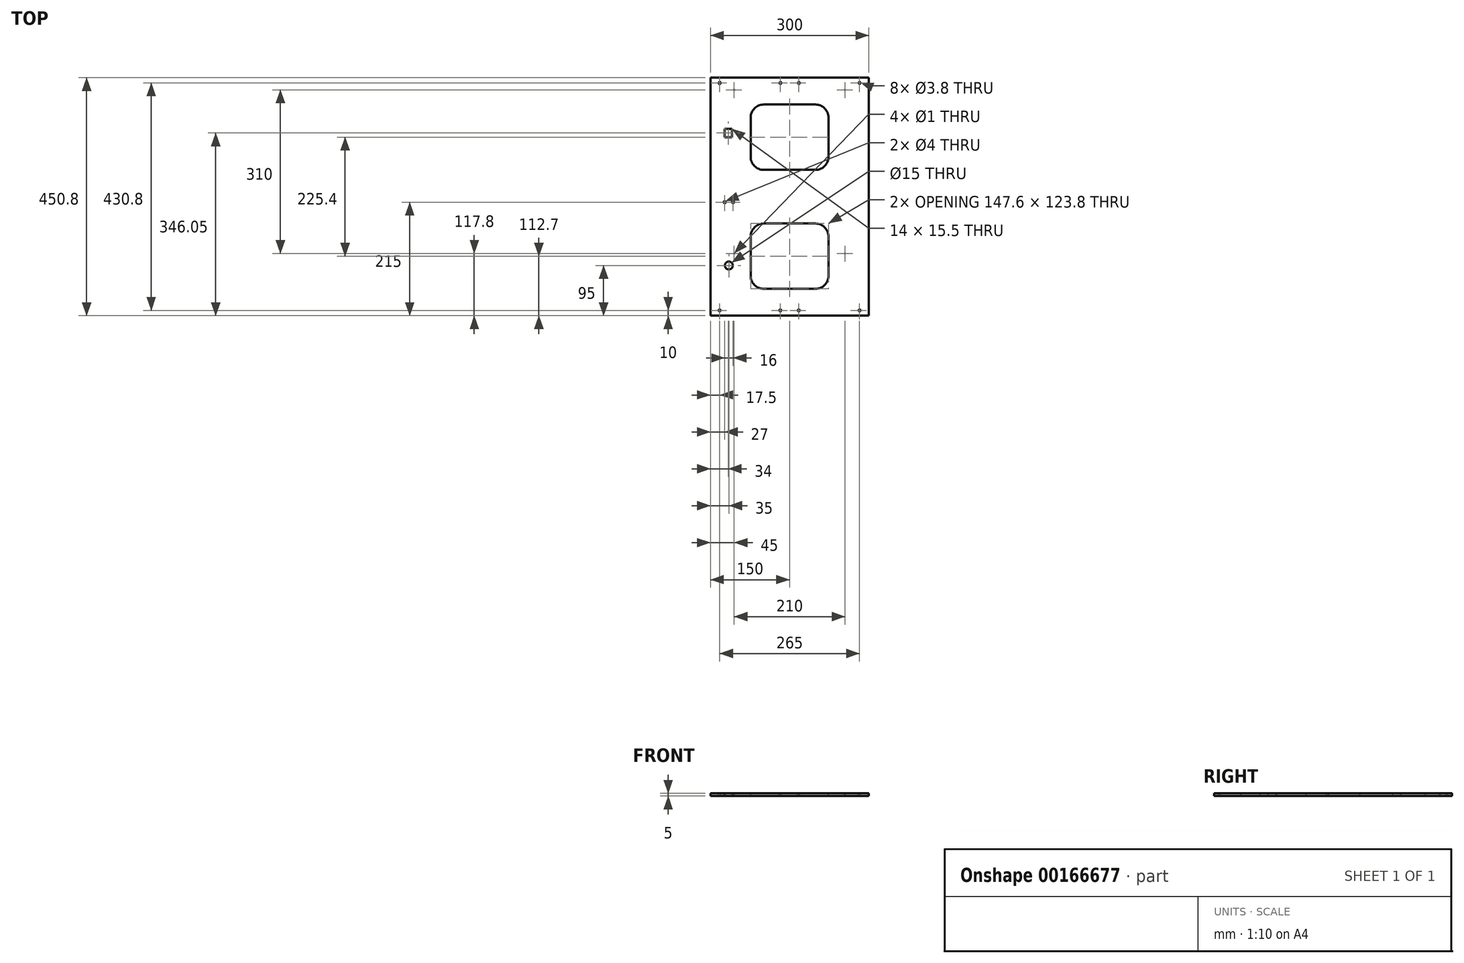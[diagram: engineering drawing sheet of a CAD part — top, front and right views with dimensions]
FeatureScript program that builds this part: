
annotation { "Feature Type Name" : "Feature", "Feature Type Description" : "" }
export const myFeature = defineFeature(function(context is Context, id is Id, definition is map)
    precondition{}
    {
        {
            var Q0;
            Q0=qCreatedBy(makeId("Top.planeOp"),FACE);
            var sketch = newSketch(context, id + "F0", { "sketchPlane" : qUnion([Q0])});
            skLineSegment(sketch, "E0.bottom", {"start": v(-150, 225.4) * mm, "end": v(150, 225.4) * mm});
            skLineSegment(sketch, "E0.top", {"start": v(-150, -225.4) * mm, "end": v(150, -225.4) * mm});
            skLineSegment(sketch, "E0.left", {"start": v(-150, 225.4) * mm, "end": v(-150, -225.4) * mm});
            skLineSegment(sketch, "E0.right", {"start": v(150, 225.4) * mm, "end": v(150, -225.4) * mm});
            skLineSegment(sketch, "E1.bottom", {"start": v(-132.5, 215.4) * mm, "end": v(132.5, 215.4) * mm, "construction": true});
            skLineSegment(sketch, "E1.top", {"start": v(-132.5, -215.4) * mm, "end": v(132.5, -215.4) * mm, "construction": true});
            skLineSegment(sketch, "E1.left", {"start": v(-132.5, 215.4) * mm, "end": v(-132.5, -215.4) * mm, "construction": true});
            skLineSegment(sketch, "E1.right", {"start": v(132.5, 215.4) * mm, "end": v(132.5, -215.4) * mm, "construction": true});
            skCircle(sketch, "E2", {"center": v(132.5, 215.4) * mm, "radius": 1.9 * mm});
            skCircle(sketch, "E3", {"center": v(132.5, -215.4) * mm, "radius": 1.9 * mm});
            skCircle(sketch, "E4", {"center": v(-132.5, -215.4) * mm, "radius": 1.9 * mm});
            skCircle(sketch, "E5", {"center": v(-132.5, 215.4) * mm, "radius": 1.9 * mm});
            skLineSegment(sketch, "E6.bottom", {"start": v(-17.5, 215.4) * mm, "end": v(17.5, 215.4) * mm, "construction": true});
            skLineSegment(sketch, "E6.top", {"start": v(-17.5, -215.4) * mm, "end": v(17.5, -215.4) * mm});
            skLineSegment(sketch, "E6.left", {"start": v(-17.5, 215.4) * mm, "end": v(-17.5, -215.4) * mm, "construction": true});
            skLineSegment(sketch, "E6.right", {"start": v(17.5, 215.4) * mm, "end": v(17.5, -215.4) * mm, "construction": true});
            skLineSegment(sketch, "E7", {"start": v(-150, 0) * mm, "end": v(150, 0) * mm, "construction": true});
            skCircle(sketch, "E8", {"center": v(-17.5, 215.4) * mm, "radius": 1.9 * mm});
            skCircle(sketch, "E9", {"center": v(17.5, 215.4) * mm, "radius": 1.9 * mm});
            skCircle(sketch, "E10", {"center": v(-17.5, -215.4) * mm, "radius": 1.9 * mm});
            skCircle(sketch, "E11", {"center": v(17.5, -215.4) * mm, "radius": 1.9 * mm});
            skSolve(sketch);
        }
        {
            var Q0;
            Q0=qCreatedBy(makeId("Top.planeOp"),FACE);
            var sketch = newSketch(context, id + "F1", { "sketchPlane" : qUnion([Q0])});
            skLineSegment(sketch, "E12.bottom", {"start": v(-110, 207.4) * mm, "end": v(110, 207.4) * mm, "construction": true});
            skLineSegment(sketch, "E12.top", {"start": v(-110, -112.6) * mm, "end": v(110, -112.6) * mm, "construction": true});
            skLineSegment(sketch, "E12.left", {"start": v(-110, 207.4) * mm, "end": v(-110, -112.6) * mm, "construction": true});
            skLineSegment(sketch, "E12.right", {"start": v(110, 207.4) * mm, "end": v(110, -112.6) * mm, "construction": true});
            skLineSegment(sketch, "E13.bottom", {"start": v(-105, 202.4) * mm, "end": v(105, 202.4) * mm, "construction": true});
            skLineSegment(sketch, "E13.top", {"start": v(-105, -107.6) * mm, "end": v(105, -107.6) * mm, "construction": true});
            skLineSegment(sketch, "E13.left", {"start": v(-105, 202.4) * mm, "end": v(-105, -107.6) * mm, "construction": true});
            skLineSegment(sketch, "E13.right", {"start": v(105, 202.4) * mm, "end": v(105, -107.6) * mm, "construction": true});
            skCircle(sketch, "E14", {"center": v(105, 202.4) * mm, "radius": 0.5 * mm});
            skCircle(sketch, "E15", {"center": v(105, -107.6) * mm, "radius": 0.5 * mm});
            skCircle(sketch, "E16", {"center": v(-105, -107.6) * mm, "radius": 0.5 * mm});
            skCircle(sketch, "E17", {"center": v(-105, 202.4) * mm, "radius": 0.5 * mm});
            skLineSegment(sketch, "E18", {"start": v(-110, 47.4) * mm, "end": v(110, 47.4) * mm, "construction": true});
            skPoint(sketch, "E18.startSnap0", {"position": v(-105, 47.4) * mm});
            skSolve(sketch);
        }
        {
            var Q0;
            Q0=makeQuery(id+"F0.imprint","IMPRINT",FACE,{"disambiguationData":[TD([[makeQuery(id+"F0.imprint","IMPRINT",EDGE,{"derivedFrom":sQuery(id+"F0.wireOp",EDGE,"E0.bottom")}),-1.0]])]});
            extrude(context, id + "F2", {"entities" : qUnion([Q0]), "oppositeDirection" : true, "depth" : 5 * mm});
        }
        {
            var Q0;
            Q0=makeQuery(id+"F1.imprint","IMPRINT",FACE,{"disambiguationData":[TD([[makeQuery(id+"F1.imprint","IMPRINT",EDGE,{"derivedFrom":sQuery(id+"F1.wireOp",EDGE,"E17")}),1.0]])]});
            var Q1;
            Q1=makeQuery(id+"F1.imprint","IMPRINT",FACE,{"disambiguationData":[TD([[makeQuery(id+"F1.imprint","IMPRINT",EDGE,{"derivedFrom":sQuery(id+"F1.wireOp",EDGE,"E14")}),1.0]])]});
            var Q2;
            Q2=makeQuery(id+"F1.imprint","IMPRINT",FACE,{"disambiguationData":[TD([[makeQuery(id+"F1.imprint","IMPRINT",EDGE,{"derivedFrom":sQuery(id+"F1.wireOp",EDGE,"E15")}),1.0]])]});
            var Q3;
            Q3=makeQuery(id+"F1.imprint","IMPRINT",FACE,{"disambiguationData":[TD([[makeQuery(id+"F1.imprint","IMPRINT",EDGE,{"derivedFrom":sQuery(id+"F1.wireOp",EDGE,"E16")}),1.0]])]});
            extrude(context, id + "F3", {"entities" : qUnion([Q0, Q1, Q2, Q3]), "operationType" : NewBodyOperationType.REMOVE, "oppositeDirection" : true, "depth" : 25 * mm});
        }
        {
            var Q0;
            Q0=makeQuery(id+"F0.imprint","IMPRINT",FACE,{"disambiguationData":[TD([[makeQuery(id+"F0.imprint","IMPRINT",EDGE,{"derivedFrom":sQuery(id+"F0.wireOp",EDGE,"E0.bottom")}),-1.0]])]});
            var sketch = newSketch(context, id + "F4", { "sketchPlane" : qUnion([Q0])});
            skLineSegment(sketch, "E19.bottom", {"start": v(-73.8, 174.6) * mm, "end": v(73.8, 174.6) * mm});
            skLineSegment(sketch, "E19.top", {"start": v(-73.8, 50.8) * mm, "end": v(73.8, 50.8) * mm});
            skLineSegment(sketch, "E19.left", {"start": v(-73.8, 174.6) * mm, "end": v(-73.8, 50.8) * mm});
            skLineSegment(sketch, "E19.right", {"start": v(73.8, 174.6) * mm, "end": v(73.8, 50.8) * mm});
            skLineSegment(sketch, "E20.bottom", {"start": v(-73.8, -50.8) * mm, "end": v(73.8, -50.8) * mm});
            skLineSegment(sketch, "E20.top", {"start": v(-73.8, -174.6) * mm, "end": v(73.8, -174.6) * mm});
            skLineSegment(sketch, "E20.left", {"start": v(-73.8, -50.8) * mm, "end": v(-73.8, -174.6) * mm});
            skLineSegment(sketch, "E20.right", {"start": v(73.8, -50.8) * mm, "end": v(73.8, -174.6) * mm});
            skLineSegment(sketch, "E21", {"start": v(-73.8, 50.8) * mm, "end": v(-73.8, -50.8) * mm, "construction": true});
            skLineSegment(sketch, "E22", {"start": v(73.8, 50.8) * mm, "end": v(73.8, -50.8) * mm, "construction": true});
            skSolve(sketch);
        }
        {
            var Q0;
            Q0=makeQuery(id+"F4.imprint","IMPRINT",FACE,{"disambiguationData":[TD([[makeQuery(id+"F4.imprint","IMPRINT",EDGE,{"derivedFrom":sQuery(id+"F4.wireOp",EDGE,"E19.bottom")}),-1.0]])]});
            var Q1;
            Q1=makeQuery(id+"F4.imprint","IMPRINT",FACE,{"disambiguationData":[TD([[makeQuery(id+"F4.imprint","IMPRINT",EDGE,{"derivedFrom":sQuery(id+"F4.wireOp",EDGE,"E20.bottom")}),-1.0]])]});
            extrude(context, id + "F5", {"entities" : qUnion([Q0, Q1]), "operationType" : NewBodyOperationType.REMOVE, "oppositeDirection" : true, "depth" : 25 * mm});
        }
        {
            var Q0;
            Q0=makeQuery(id+"F5.boolean.opBoolean","COPY",EDGE,{"derivedFrom":makeQuery(id+"F5.opExtrude","SWEPT_EDGE",EDGE,{"disambiguationData":[OSD([sQuery(id+"F4.wireOp",EDGE,"E19.bottom"),sQuery(id+"F4.wireOp",EDGE,"E19.left")])]})});
            var Q1;
            Q1=makeQuery(id+"F5.boolean.opBoolean","COPY",EDGE,{"derivedFrom":makeQuery(id+"F5.opExtrude","SWEPT_EDGE",EDGE,{"disambiguationData":[OSD([sQuery(id+"F4.wireOp",EDGE,"E19.bottom"),sQuery(id+"F4.wireOp",EDGE,"E19.right")])]})});
            var Q2;
            Q2=makeQuery(id+"F5.boolean.opBoolean","COPY",EDGE,{"derivedFrom":makeQuery(id+"F5.opExtrude","SWEPT_EDGE",EDGE,{"disambiguationData":[OSD([sQuery(id+"F4.wireOp",EDGE,"E19.top"),sQuery(id+"F4.wireOp",EDGE,"E19.left")])]})});
            var Q3;
            Q3=makeQuery(id+"F5.boolean.opBoolean","COPY",EDGE,{"derivedFrom":makeQuery(id+"F5.opExtrude","SWEPT_EDGE",EDGE,{"disambiguationData":[OSD([sQuery(id+"F4.wireOp",EDGE,"E19.top"),sQuery(id+"F4.wireOp",EDGE,"E19.right")])]})});
            var Q4;
            Q4=makeQuery(id+"F5.boolean.opBoolean","COPY",EDGE,{"derivedFrom":makeQuery(id+"F5.opExtrude","SWEPT_EDGE",EDGE,{"disambiguationData":[OSD([sQuery(id+"F4.wireOp",EDGE,"E20.bottom"),sQuery(id+"F4.wireOp",EDGE,"E20.left")])]})});
            var Q5;
            Q5=makeQuery(id+"F5.boolean.opBoolean","COPY",EDGE,{"derivedFrom":makeQuery(id+"F5.opExtrude","SWEPT_EDGE",EDGE,{"disambiguationData":[OSD([sQuery(id+"F4.wireOp",EDGE,"E20.bottom"),sQuery(id+"F4.wireOp",EDGE,"E20.right")])]})});
            var Q6;
            Q6=makeQuery(id+"F5.boolean.opBoolean","COPY",EDGE,{"derivedFrom":makeQuery(id+"F5.opExtrude","SWEPT_EDGE",EDGE,{"disambiguationData":[OSD([sQuery(id+"F4.wireOp",EDGE,"E20.top"),sQuery(id+"F4.wireOp",EDGE,"E20.right")])]})});
            var Q7;
            Q7=makeQuery(id+"F5.boolean.opBoolean","COPY",EDGE,{"derivedFrom":makeQuery(id+"F5.opExtrude","SWEPT_EDGE",EDGE,{"disambiguationData":[OSD([sQuery(id+"F4.wireOp",EDGE,"E20.top"),sQuery(id+"F4.wireOp",EDGE,"E20.left")])]})});
            fillet(context, id + "F6", {"entities" : qUnion([Q0, Q1, Q2, Q3, Q4, Q5, Q6, Q7]), "radius" : 25 * mm, "tangentPropagation" : true, "allowEdgeOverflow" : false});
        }
        {
            var Q0;
            Q0=makeQuery(id+"F2.opExtrude","CAP_FACE",FACE,{"disambiguationData":[OSD([sQuery(id+"F0.wireOp",EDGE,"E0.bottom"),sQuery(id+"F0.wireOp",EDGE,"E0.top"),sQuery(id+"F0.wireOp",EDGE,"E0.left"),sQuery(id+"F0.wireOp",EDGE,"E0.right"),sQuery(id+"F0.wireOp",EDGE,"E2"),sQuery(id+"F0.wireOp",EDGE,"E3"),sQuery(id+"F0.wireOp",EDGE,"E4"),sQuery(id+"F0.wireOp",EDGE,"E5"),sQuery(id+"F0.wireOp",EDGE,"E8"),sQuery(id+"F0.wireOp",EDGE,"E9"),sQuery(id+"F0.wireOp",EDGE,"E10"),sQuery(id+"F0.wireOp",EDGE,"E11")])],"isStart":true});
            var sketch = newSketch(context, id + "F7", { "sketchPlane" : qUnion([Q0])});
            skLineSegment(sketch, "E23.bottom", {"start": v(-123, 128.4) * mm, "end": v(-109, 128.4) * mm});
            skLineSegment(sketch, "E23.top", {"start": v(-123, 112.9) * mm, "end": v(-109, 112.9) * mm});
            skLineSegment(sketch, "E23.left", {"start": v(-123, 128.4) * mm, "end": v(-123, 112.9) * mm});
            skLineSegment(sketch, "E23.right", {"start": v(-109, 128.4) * mm, "end": v(-109, 112.9) * mm});
            skSolve(sketch);
        }
        {
            var Q0;
            Q0=makeQuery(id+"F7.imprint","IMPRINT",FACE,{"disambiguationData":[TD([[makeQuery(id+"F7.imprint","IMPRINT",EDGE,{"derivedFrom":sQuery(id+"F7.wireOp",EDGE,"E23.bottom")}),-1.0]])]});
            extrude(context, id + "F8", {"entities" : qUnion([Q0]), "operationType" : NewBodyOperationType.REMOVE, "oppositeDirection" : true, "depth" : 25 * mm});
        }
        {
            var Q0;
            Q0=makeQuery(id+"F7.imprint","IMPRINT",FACE,{"disambiguationData":[TD([[makeQuery(id+"F7.imprint","IMPRINT",EDGE,{"derivedFrom":sQuery(id+"F7.wireOp",EDGE,"E23.bottom")}),1.0]])]});
            var sketch = newSketch(context, id + "F9", { "sketchPlane" : qUnion([Q0])});
            skLineSegment(sketch, "E24", {"start": v(-115, -225.4) * mm, "end": v(-115, 225.4) * mm, "construction": true});
            skCircle(sketch, "E25", {"center": v(-115, -130.4) * mm, "radius": 7.5 * mm});
            skLineSegment(sketch, "E26", {"start": v(-123, -10.4) * mm, "end": v(-107, -10.4) * mm, "construction": true});
            skCircle(sketch, "E27", {"center": v(-107, -10.4) * mm, "radius": 2 * mm});
            skCircle(sketch, "E28", {"center": v(-123, -10.4) * mm, "radius": 2 * mm});
            skSolve(sketch);
        }
        {
            var Q0;
            Q0=makeQuery(id+"F9.imprint","IMPRINT",FACE,{"disambiguationData":[TD([[makeQuery(id+"F9.imprint","IMPRINT",EDGE,{"derivedFrom":sQuery(id+"F9.wireOp",EDGE,"E25")}),1.0]])]});
            extrude(context, id + "F10", {"entities" : qUnion([Q0]), "operationType" : NewBodyOperationType.REMOVE, "oppositeDirection" : true, "depth" : 25 * mm});
        }
        {
            var Q0;
            Q0=makeQuery(id+"F9.imprint","IMPRINT",FACE,{"disambiguationData":[TD([[makeQuery(id+"F9.imprint","IMPRINT",EDGE,{"derivedFrom":sQuery(id+"F9.wireOp",EDGE,"E27")}),1.0]])]});
            var Q1;
            Q1=makeQuery(id+"F9.imprint","IMPRINT",FACE,{"disambiguationData":[TD([[makeQuery(id+"F9.imprint","IMPRINT",EDGE,{"derivedFrom":sQuery(id+"F9.wireOp",EDGE,"E28")}),1.0]])]});
            extrude(context, id + "F11", {"entities" : qUnion([Q0, Q1]), "operationType" : NewBodyOperationType.REMOVE, "oppositeDirection" : true, "depth" : 25 * mm});
        }
    });
